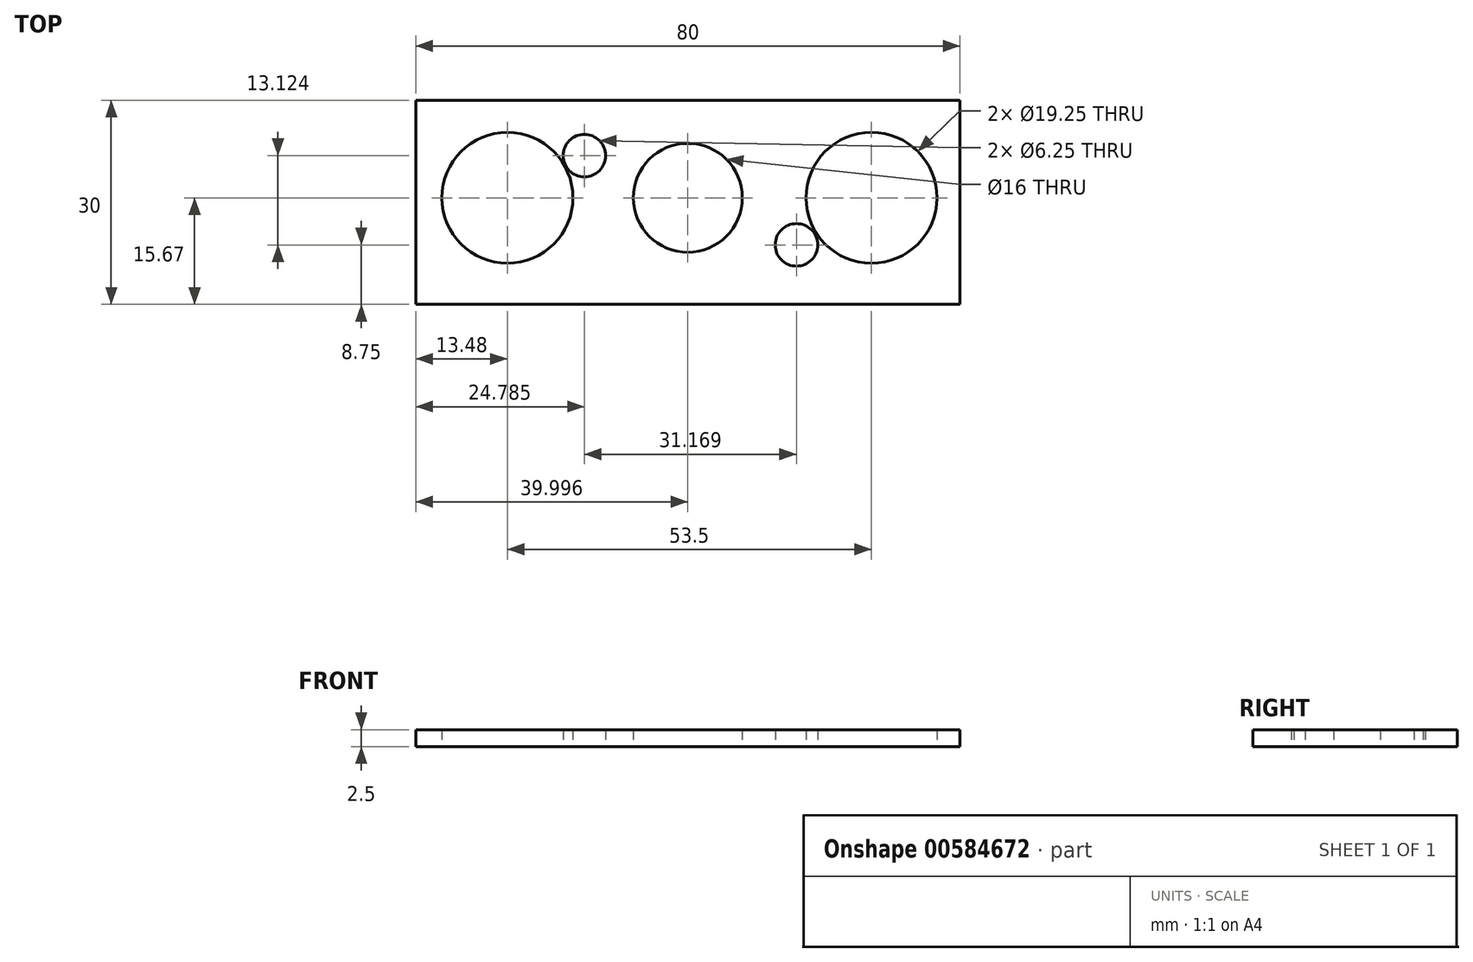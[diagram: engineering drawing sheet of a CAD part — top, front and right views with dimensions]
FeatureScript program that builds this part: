
annotation { "Feature Type Name" : "Feature", "Feature Type Description" : "" }
export const myFeature = defineFeature(function(context is Context, id is Id, definition is map)
    precondition{}
    {
        {
            var Q0;
            Q0=qCreatedBy(makeId("Top.planeOp"),FACE);
            var sketch = newSketch(context, id + "F0", { "sketchPlane" : qUnion([Q0])});
            skCircle(sketch, "E0", {"center": v(0, 0) * mm, "radius": 9.62 * mm});
            skCircle(sketch, "E1", {"center": v(-53.5, 0) * mm, "radius": 9.62 * mm});
            skLineSegment(sketch, "E2.bottom", {"start": v(-66.98, 14.33) * mm, "end": v(13.02, 14.33) * mm});
            skLineSegment(sketch, "E2.top", {"start": v(-66.98, -15.67) * mm, "end": v(13.02, -15.67) * mm});
            skLineSegment(sketch, "E2.left", {"start": v(-66.98, 14.33) * mm, "end": v(-66.98, -15.67) * mm});
            skLineSegment(sketch, "E2.right", {"start": v(13.02, 14.33) * mm, "end": v(13.02, -15.67) * mm});
            skCircle(sketch, "E3", {"center": v(-26.98, 0) * mm, "radius": 8 * mm});
            skPoint(sketch, "E4", {"position": v(-26.98, -15.67) * mm});
            skCircle(sketch, "E5", {"center": v(-11.03, -6.92) * mm, "radius": 3.12 * mm});
            skCircle(sketch, "E6", {"center": v(-42.2, 6.2) * mm, "radius": 3.12 * mm});
            skSolve(sketch);
        }
        {
            var Q0;
            Q0=makeQuery(id+"F0.imprint","IMPRINT",FACE,{"disambiguationData":[TD([[makeQuery(id+"F0.imprint","IMPRINT",EDGE,{"derivedFrom":sQuery(id+"F0.wireOp",EDGE,"E0")}),-1.0]])]});
            extrude(context, id + "F1", {"entities" : qUnion([Q0]), "depth" : 2.5 * mm, "offsetDistance" : 25 * mm});
        }
    });
